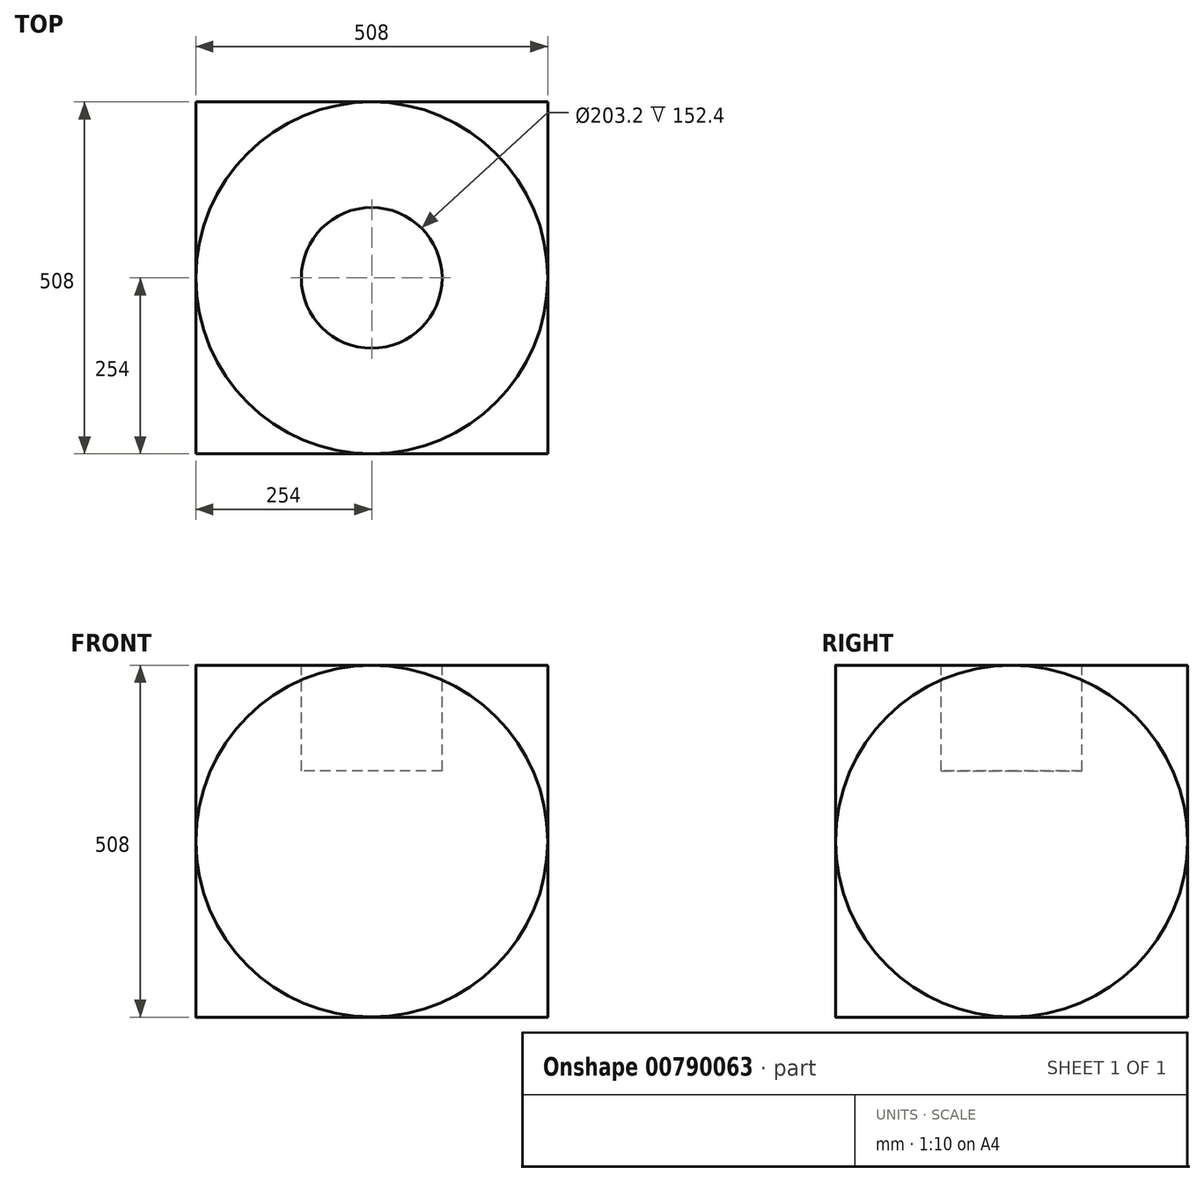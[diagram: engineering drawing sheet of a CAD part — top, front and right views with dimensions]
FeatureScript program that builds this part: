
annotation { "Feature Type Name" : "Feature", "Feature Type Description" : "" }
export const myFeature = defineFeature(function(context is Context, id is Id, definition is map)
    precondition{}
    {
        {
            var Q0;
            Q0=qCreatedBy(makeId("Front.planeOp"),FACE);
            var sketch = newSketch(context, id + "F0", { "sketchPlane" : qUnion([Q0])});
            skLineSegment(sketch, "E0", {"start": v(0, 0) * mm, "end": v(359.16, 0) * mm});
            skLineSegment(sketch, "E1", {"start": v(0, 0) * mm, "end": v(-359.16, 0) * mm});
            skArc(sketch, "E2", {"start": v(359.16, 0) * mm, "mid": v(0, 359.16) * mm, "end": v(-359.16, 0) * mm});
            skSolve(sketch);
        }
        {
            var Q0;
            Q0=makeQuery(id+"F0.imprint","IMPRINT",FACE,{"disambiguationData":[TD([[makeQuery(id+"F0.imprint","IMPRINT",EDGE,{"derivedFrom":sQuery(id+"F0.wireOp",EDGE,"E0")}),1.0]])]});
            var Q1;
            Q1=sQuery(id+"F0.wireOp",EDGE,"E0");
            revolve(context, id + "F1", {"surfaceOperationType" : NewSurfaceOperationType.NEW, "entities" : qUnion([Q0]), "axis" : qUnion([Q1]), "revolveType" : RevolveType.FULL});
        }
        {
            var Q0;
            Q0=qCreatedBy(makeId("Front.planeOp"),FACE);
            cPlane(context, id + "F2", {"entities" : qUnion([Q0]), "cplaneType" : CPlaneType.OFFSET, "offset" : 254 * mm, "width" : 152.4 * mm, "height" : 152.4 * mm});
        }
        {
            var Q0;
            Q0=qCreatedBy(id+"F2.planeOp",FACE);
            var sketch = newSketch(context, id + "F3", { "sketchPlane" : qUnion([Q0])});
            skLineSegment(sketch, "E3.bottom", {"start": v(-487.73, 723.13) * mm, "end": v(403, 723.13) * mm});
            skLineSegment(sketch, "E3.top", {"start": v(-487.73, -596.1) * mm, "end": v(403, -596.1) * mm});
            skLineSegment(sketch, "E3.left", {"start": v(-487.73, 723.13) * mm, "end": v(-487.73, -596.1) * mm});
            skLineSegment(sketch, "E3.right", {"start": v(403, 723.13) * mm, "end": v(403, -596.1) * mm});
            skSolve(sketch);
        }
        {
            var Q0;
            Q0=makeQuery(id+"F3.imprint","IMPRINT",FACE,{"disambiguationData":[TD([[makeQuery(id+"F3.imprint","IMPRINT",EDGE,{"derivedFrom":sQuery(id+"F3.wireOp",EDGE,"E3.bottom")}),-1.0]])]});
            extrude(context, id + "F4", {"entities" : qUnion([Q0]), "operationType" : NewBodyOperationType.REMOVE, "depth" : 254 * mm, "offsetDistance" : 25.4 * mm});
        }
        {
            var Q0;
            Q0=qCreatedBy(id+"F2.planeOp",FACE);
            cPlane(context, id + "F5", {"entities" : qUnion([Q0]), "cplaneType" : CPlaneType.OFFSET, "offset" : 508 * mm, "oppositeDirection" : true, "width" : 152.4 * mm, "height" : 152.4 * mm});
        }
        {
            var Q0;
            Q0=qCreatedBy(id+"F5.planeOp",FACE);
            var sketch = newSketch(context, id + "F6", { "sketchPlane" : qUnion([Q0])});
            skLineSegment(sketch, "E4.bottom", {"start": v(415.9, -514.35) * mm, "end": v(-596.46, -514.35) * mm});
            skLineSegment(sketch, "E4.top", {"start": v(415.9, 776.23) * mm, "end": v(-596.46, 776.23) * mm});
            skLineSegment(sketch, "E4.left", {"start": v(415.9, -514.35) * mm, "end": v(415.9, 776.23) * mm});
            skLineSegment(sketch, "E4.right", {"start": v(-596.46, -514.35) * mm, "end": v(-596.46, 776.23) * mm});
            skSolve(sketch);
        }
        {
            var Q0;
            Q0=makeQuery(id+"F6.imprint","IMPRINT",FACE,{"disambiguationData":[TD([[makeQuery(id+"F6.imprint","IMPRINT",EDGE,{"derivedFrom":sQuery(id+"F6.wireOp",EDGE,"E4.bottom")}),-1.0]])]});
            extrude(context, id + "F7", {"entities" : qUnion([Q0]), "operationType" : NewBodyOperationType.REMOVE, "oppositeDirection" : true, "depth" : 254 * mm, "offsetDistance" : 25.4 * mm});
        }
        {
            var Q0;
            Q0=qCreatedBy(makeId("Top.planeOp"),FACE);
            cPlane(context, id + "F8", {"entities" : qUnion([Q0]), "cplaneType" : CPlaneType.OFFSET, "offset" : 254 * mm, "width" : 152.4 * mm, "height" : 152.4 * mm});
        }
        {
            var Q0;
            Q0=qCreatedBy(id+"F8.planeOp",FACE);
            var sketch = newSketch(context, id + "F9", { "sketchPlane" : qUnion([Q0])});
            skLineSegment(sketch, "E5.bottom", {"start": v(675.52, -615.08) * mm, "end": v(446.44, -615.08) * mm});
            skLineSegment(sketch, "E5.top", {"start": v(675.52, -508.59) * mm, "end": v(446.44, -508.59) * mm});
            skLineSegment(sketch, "E5.left", {"start": v(675.52, -615.08) * mm, "end": v(675.52, -508.59) * mm});
            skLineSegment(sketch, "E5.right", {"start": v(446.44, -615.08) * mm, "end": v(446.44, -508.59) * mm});
            skLineSegment(sketch, "E6.bottom", {"start": v(456.42, -515.4) * mm, "end": v(-582.26, -515.4) * mm});
            skLineSegment(sketch, "E6.top", {"start": v(456.42, 446.42) * mm, "end": v(-582.26, 446.42) * mm});
            skLineSegment(sketch, "E6.left", {"start": v(456.42, -515.4) * mm, "end": v(456.42, 446.42) * mm});
            skLineSegment(sketch, "E6.right", {"start": v(-582.26, -515.4) * mm, "end": v(-582.26, 446.42) * mm});
            skSolve(sketch);
        }
        {
            var Q0;
            {var subQ0=sQuery(id+"F9.wireOp",EDGE,"E6.top");Q0=makeQuery(id+"F9.imprint","IMPRINT",FACE,{"disambiguationData":[TD([[makeQuery(id+"F9.imprint","IMPRINT",EDGE,{"derivedFrom":subQ0}),1.0]])]});}
            extrude(context, id + "F10", {"entities" : qUnion([Q0]), "operationType" : NewBodyOperationType.REMOVE, "depth" : 254 * mm, "offsetDistance" : 25.4 * mm});
        }
        {
            var Q0;
            Q0=qCreatedBy(id+"F8.planeOp",FACE);
            cPlane(context, id + "F11", {"entities" : qUnion([Q0]), "cplaneType" : CPlaneType.OFFSET, "offset" : 508 * mm, "oppositeDirection" : true, "width" : 152.4 * mm, "height" : 152.4 * mm});
        }
        {
            var Q0;
            Q0=qCreatedBy(id+"F11.planeOp",FACE);
            var sketch = newSketch(context, id + "F12", { "sketchPlane" : qUnion([Q0])});
            skLineSegment(sketch, "E7.bottom", {"start": v(717.56, -517.53) * mm, "end": v(-552.99, -517.53) * mm});
            skLineSegment(sketch, "E7.top", {"start": v(717.56, 679.15) * mm, "end": v(-552.99, 679.15) * mm});
            skLineSegment(sketch, "E7.left", {"start": v(717.56, -517.53) * mm, "end": v(717.56, 679.15) * mm});
            skLineSegment(sketch, "E7.right", {"start": v(-552.99, -517.53) * mm, "end": v(-552.99, 679.15) * mm});
            skSolve(sketch);
        }
        {
            var Q0;
            Q0=makeQuery(id+"F12.imprint","IMPRINT",FACE,{"disambiguationData":[TD([[makeQuery(id+"F12.imprint","IMPRINT",EDGE,{"derivedFrom":sQuery(id+"F12.wireOp",EDGE,"E7.bottom")}),-1.0]])]});
            extrude(context, id + "F13", {"entities" : qUnion([Q0]), "operationType" : NewBodyOperationType.REMOVE, "oppositeDirection" : true, "depth" : 254 * mm, "offsetDistance" : 25.4 * mm});
        }
        {
            var Q0;
            Q0=qCreatedBy(makeId("Right.planeOp"),FACE);
            cPlane(context, id + "F14", {"entities" : qUnion([Q0]), "cplaneType" : CPlaneType.OFFSET, "offset" : 254 * mm, "oppositeDirection" : true, "width" : 152.4 * mm, "height" : 152.4 * mm});
        }
        {
            var Q0;
            Q0=qCreatedBy(id+"F14.planeOp",FACE);
            var sketch = newSketch(context, id + "F15", { "sketchPlane" : qUnion([Q0])});
            skLineSegment(sketch, "E8.bottom", {"start": v(420.15, 626.4) * mm, "end": v(-530.83, 626.4) * mm});
            skLineSegment(sketch, "E8.top", {"start": v(420.15, -1261.57) * mm, "end": v(-530.83, -1261.57) * mm});
            skLineSegment(sketch, "E8.left", {"start": v(420.15, 626.4) * mm, "end": v(420.15, -1261.57) * mm});
            skLineSegment(sketch, "E8.right", {"start": v(-530.83, 626.4) * mm, "end": v(-530.83, -1261.57) * mm});
            skSolve(sketch);
        }
        {
            var Q0;
            Q0=makeQuery(id+"F15.imprint","IMPRINT",FACE,{"disambiguationData":[TD([[makeQuery(id+"F15.imprint","IMPRINT",EDGE,{"derivedFrom":sQuery(id+"F15.wireOp",EDGE,"E8.bottom")}),1.0]])]});
            extrude(context, id + "F16", {"entities" : qUnion([Q0]), "operationType" : NewBodyOperationType.REMOVE, "oppositeDirection" : true, "depth" : 254 * mm, "offsetDistance" : 25.4 * mm});
        }
        {
            var Q0;
            Q0=qCreatedBy(makeId("Right.planeOp"),FACE);
            cPlane(context, id + "F17", {"entities" : qUnion([Q0]), "cplaneType" : CPlaneType.OFFSET, "offset" : 254 * mm, "width" : 152.4 * mm, "height" : 152.4 * mm});
        }
        {
            var Q0;
            Q0=qCreatedBy(id+"F17.planeOp",FACE);
            var sketch = newSketch(context, id + "F18", { "sketchPlane" : qUnion([Q0])});
            skLineSegment(sketch, "E9.bottom", {"start": v(-499.59, 1077.45) * mm, "end": v(-462.63, 1077.45) * mm});
            skLineSegment(sketch, "E9.top", {"start": v(-499.59, 1110.26) * mm, "end": v(-462.63, 1110.26) * mm});
            skLineSegment(sketch, "E9.left", {"start": v(-499.59, 1077.45) * mm, "end": v(-499.59, 1110.26) * mm});
            skLineSegment(sketch, "E9.right", {"start": v(-462.63, 1077.45) * mm, "end": v(-462.63, 1110.26) * mm});
            skLineSegment(sketch, "E10.bottom", {"start": v(-462.63, 1110.26) * mm, "end": v(636.58, 1110.26) * mm});
            skLineSegment(sketch, "E10.top", {"start": v(-462.63, -1249.09) * mm, "end": v(636.58, -1249.09) * mm});
            skLineSegment(sketch, "E10.left", {"start": v(-462.63, 1110.26) * mm, "end": v(-462.63, -1249.09) * mm});
            skLineSegment(sketch, "E10.right", {"start": v(636.58, 1110.26) * mm, "end": v(636.58, -1249.09) * mm});
            skSolve(sketch);
        }
        {
            var Q0;
            {var subQ3=sQuery(id+"F18.wireOp",EDGE,"E10.bottom");Q0=makeQuery(id+"F18.imprint","IMPRINT",FACE,{"disambiguationData":[TD([[makeQuery(id+"F18.imprint","IMPRINT",EDGE,{"derivedFrom":subQ3}),-1.0]])]});}
            extrude(context, id + "F19", {"entities" : qUnion([Q0]), "operationType" : NewBodyOperationType.REMOVE, "depth" : 254 * mm, "offsetDistance" : 25.4 * mm});
        }
        {
            var Q0;
            Q0=makeQuery(id+"F10.boolean.opBoolean","COPY",FACE,{"derivedFrom":makeQuery(id+"F10.opExtrude","CAP_FACE",FACE,{"disambiguationData":[OSD([sQuery(id+"F9.wireOp",EDGE,"E5.top"),sQuery(id+"F9.wireOp",EDGE,"E5.right"),sQuery(id+"F9.wireOp",EDGE,"E6.bottom"),sQuery(id+"F9.wireOp",EDGE,"E6.top"),sQuery(id+"F9.wireOp",EDGE,"E6.left"),sQuery(id+"F9.wireOp",EDGE,"E6.right")])],"isStart":true})});
            var sketch = newSketch(context, id + "F20", { "sketchPlane" : qUnion([Q0])});
            skCircle(sketch, "E11", {"center": v(0, 0) * mm, "radius": 101.6 * mm});
            skSolve(sketch);
        }
        {
            var Q0;
            Q0=makeQuery(id+"F20.imprint","IMPRINT",FACE,{"disambiguationData":[TD([[makeQuery(id+"F20.imprint","IMPRINT",EDGE,{"derivedFrom":sQuery(id+"F20.wireOp",EDGE,"E11")}),1.0]])]});
            var Q1;
            Q1=sQuery(id+"F20.wireOp",EDGE,"E11");
            extrude(context, id + "F21", {"entities" : qUnion([Q0]), "operationType" : NewBodyOperationType.REMOVE, "surfaceEntities" : qUnion([Q1]), "oppositeDirection" : true, "depth" : 152.4 * mm, "offsetDistance" : 25.4 * mm});
        }
    });
